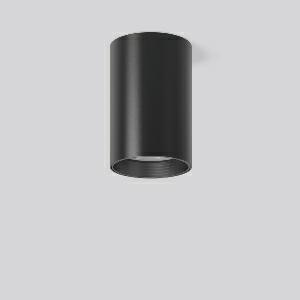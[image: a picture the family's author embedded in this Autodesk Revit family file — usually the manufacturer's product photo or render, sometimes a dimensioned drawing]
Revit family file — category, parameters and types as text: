
# Revit family: heledon_maxi_a_931222_003_3_76_958e
name_source: partatom
category: Lighting Fixtures
units: mm (PartAtom-declared; Revit-internal decimal feet)

## family parameters
Cut with Voids When Loaded = No
Host = Face
Light Source = No
Part Type = Normal
Room Calculation Point = No
Round Connector Dimension = Use Diameter
Shared = No

## types (1)
- HELEDON maxi A (1 x LED Modul 935, 2850 lm, 3500)
    Apparent Load = 25 VA
    Approval mark = CE
    CIE Flux Codes = 96 100 100 100 100
    Color Rendering = 92
    Color Temperature = 3500
    Default Elevation = 1800 mm
    Description = Series: HELEDON maxi
Cylindrical surface-mounted downlight. Housing: die-cast aluminium, powder-coated. Internal ceiling frame polycarbonate with bayonet mounting. Black plastic ring and recessed LED to prevent glare from the side. Optical assembly with lens made of plastic (polycarbonate) for the best homogeneous light distribution - can be changed without tools. Best colour rendering index Ra>90. Suitable for Ceiling mounting. Easy installation with a separate ceiling frame with bayonet mounting and plug connection. Driver integrated. Connected via plug-in connector. High quality converter without flickering and stroboscopic effect. The following accessories can be mounted without use of tools: interchangeable lenses, decorative glasses, honeycomb louvre, clear and frosted diffusers, white interchangeable plastic ring. 
Colour: deep black, matt (RAL 9005)
Diameter: 123 mm
Height: 183 mm
Lamp: LED
Socket: without socket
Colour temperature: 3500K
Colour rendering index (CRI): 92
System power: 25 W
Rated luminous flux: 2850 lm
Luminous efficiency: 114 lm/W
Control gear: Converter, dimmable, DALI
Protection class: I
Type of protection: IP 20
    Height = 183 mm
    Lamp = 1 x LED Modul 935
    Lamp Light Flux = 2850 lm
    Lamp count = 1
    Length = 123 mm
    Lifetime = 50000 h
    Luminous efficacy = 114 lm/W
    Manufacturer = RZB
    ModVariant = No
    Model = 931222.003.3.76
    Mounting Place = Ceiling
    Mounting Type = Surface mounted
    Number of Poles = 1
    OnlyDefault = Yes
    Power Factor = 1
    Product Name = HELEDON maxi A
    Product group = Surface mounted downlights
    ProductGroupID = 302
    Protection Class = Protection class I
    Protection Degree = IP 20
    RLX_Detail_Level = 1
    RLX_Emergency_Light_Flux = 0 lm
    RLX_Emergency_Type = 0
    RLX_Emergency_Type_DB = No
    RlxData = <blob elided: 96497 chars, md5=61b9a60f>
    Socket = socket
    Standby Power = 0 W
    System Light Flux = 2850 lm
    System Power = 25 W
    Type Comments = Product without accessories
    Type Image = 931193.003.jpg
    URL = http://relux.com
    VarID = ---
    Voltage = 230 V
    Voltage Range = 220-240 V
    Weight = 0.00 kg
    Width = 0 mm  [stored 0 ft]

note: [stored X ft] marks values corroborated as IEEE doubles in the binary element streams (Revit-internal decimal feet)

## geometry (parser evidence)
native form markers: Blend x4, Sweep x11
no freeform markers — native parametric forms only
